# Revit family: STH8940BR_STH8940BRPTO_STH8940PTO
name_source: partatom
category: Luminárias
units: mm (PartAtom-declared; Revit-internal decimal feet)

## family parameters
Compartilhado = Não
Corte com vazios quando carregada = Não
Cota do conector redondo = Utilizar diâmetro
Fonte luminosa = Não
Hospedeiro = Forro
Manter orientação da anotação = Não
Número OmniClass = 23.80.70.11
Ponto de cálculo do ambiente = Não
Sempre na vertical = Sim
Tipo de parte = Normal
Título OmniClass = Luminaries for Internal Lighting

## types (3) — shared parameters
Altura = 0.08 m
Comentários de tipos = Lâmpada indicada: 1x MR11 GU10 Stella.
Comprimento = 0.07 m
Estrutura Topo = Al - Preto
Fabricante = Stella
Fundo_Branco = Al - Branco
Fundo_Preto = Al - Preto
Largura = 0.07 m
Modelo = Square Ghost MR11
Potência máxima = 15 W
Tensão Elétrica = 127V-220V
Topo_Preto = Não
URL = https://stella.com.br
zero-valued in all types: Elevação padrão

## per-type parameters (varying)
| type | Estrutura | Flange Branca | Flange Preta | Fundo Branco | Fundo Preto | Referência |
| STH8940BR/PTO - BIVOLT | Al - Branco | Sim | Não | Não | Sim | STH8940BR/PTO |
| STH8940PTO - BIVOLT | Al - Preto | Não | Sim | Não | Sim | STH8940PTO |
| STH8940BR - BIVOLT | Al - Branco | Sim | Não | Sim | Não | STH8940BR |
